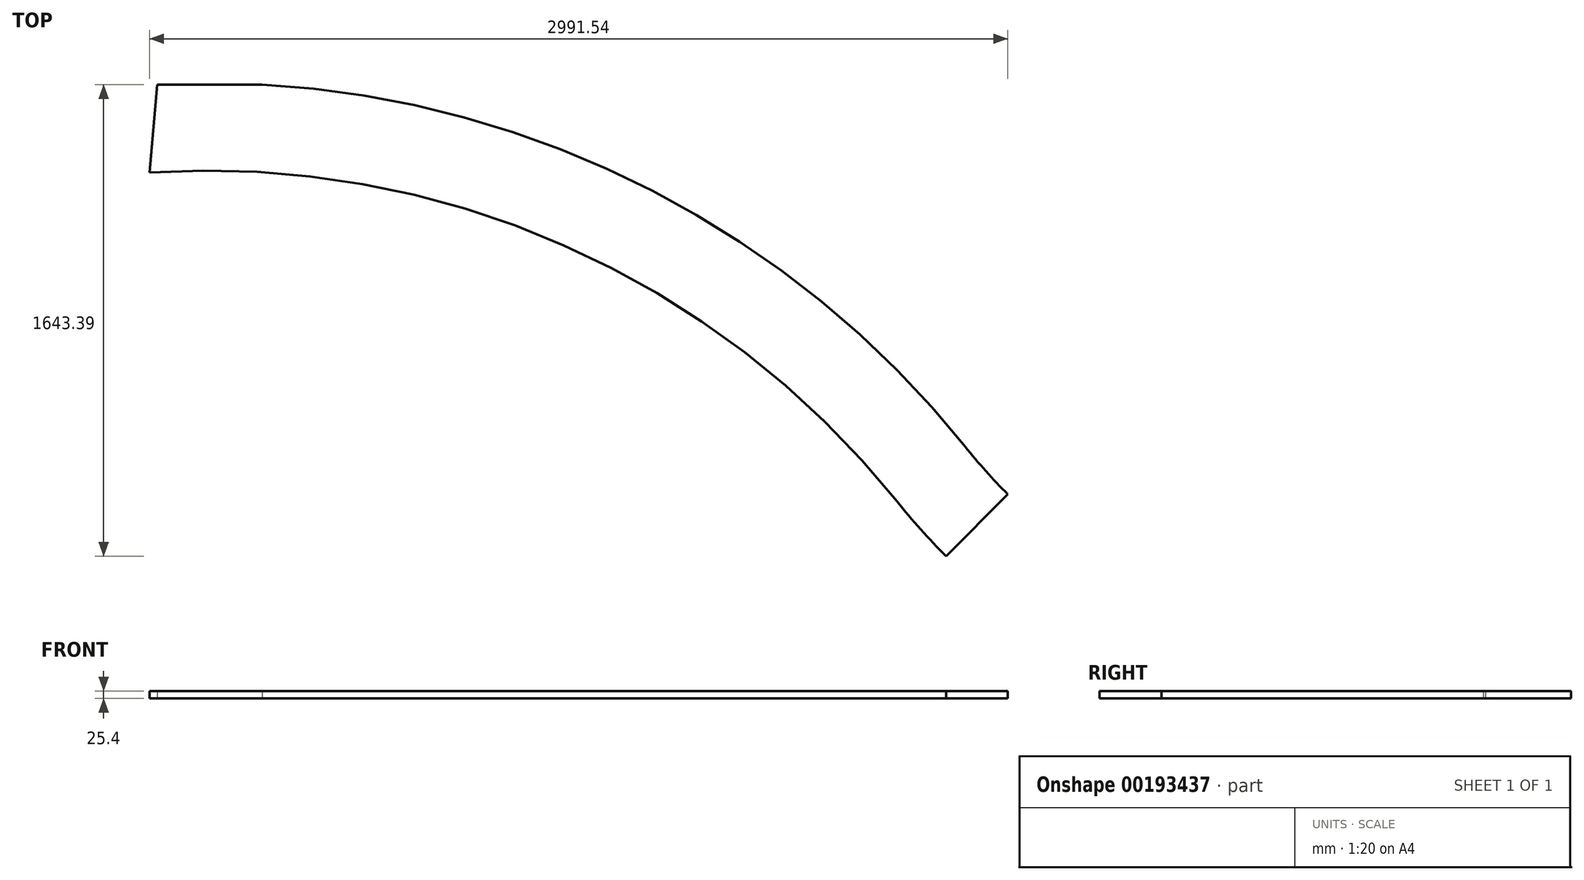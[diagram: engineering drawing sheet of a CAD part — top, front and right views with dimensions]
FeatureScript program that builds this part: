
annotation { "Feature Type Name" : "Feature", "Feature Type Description" : "" }
export const myFeature = defineFeature(function(context is Context, id is Id, definition is map)
    precondition{}
    {
        {
            var Q0;
            Q0=qCreatedBy(makeId("Top.planeOp"),FACE);
            var sketch = newSketch(context, id + "F0", { "sketchPlane" : qUnion([Q0])});
            skLineSegment(sketch, "E0", {"start": v(-2322.3, 99.74) * mm, "end": v(363.78, 99.74) * mm});
            skLineSegment(sketch, "E1", {"start": v(2078.28, -1614.76) * mm, "end": v(2078.28, -2224.36) * mm});
            skArc(sketch, "E2", {"start": v(2078.28, -1614.76) * mm, "mid": v(865.95, -1112.6) * mm, "end": v(363.78, 99.74) * mm});
            skArc(sketch, "E3.0", {"start": v(2078.28, -1919.56) * mm, "mid": v(1203.8, -1720.4) * mm, "end": v(501.84, -1162.16) * mm});
            skArc(sketch, "E4.0", {"start": v(2078.28, -2224.36) * mm, "mid": v(1071.81, -1995.13) * mm, "end": v(263.88, -1352.64) * mm});
            skLineSegment(sketch, "E5", {"start": v(-2322.3, 99.74) * mm, "end": v(-2341.12, -206.78) * mm});
            skPoint(sketch, "E6", {"position": v(-2322.3, 99.74) * mm});
            skArc(sketch, "E7", {"start": v(501.84, -1162.16) * mm, "mid": v(-757.31, -188.98) * mm, "end": v(-2322.3, 99.74) * mm});
            skArc(sketch, "E8.0", {"start": v(263.88, -1352.64) * mm, "mid": v(-898, -460.02) * mm, "end": v(-2341.12, -206.78) * mm});
            skPoint(sketch, "E9.orphan", {"position": v(-2399.79, -1162.16) * mm});
            skLineSegment(sketch, "E10", {"start": v(2078.28, 99.74) * mm, "end": v(0, -1978.55) * mm});
            skLineSegment(sketch, "E11", {"start": v(-2341.12, -206.78) * mm, "end": v(-2322.3, 99.74) * mm});
            skLineSegment(sketch, "E12", {"start": v(2078.28, -1614.76) * mm, "end": v(2052.9, -1614.09) * mm});
            skLineSegment(sketch, "E13.0", {"start": v(2052.88, -1614.09) * mm, "end": v(2052.88, -2223.26) * mm});
            skLineSegment(sketch, "E14", {"start": v(-2339.55, -181.22) * mm, "end": v(-2322.3, 99.74) * mm});
            skLineSegment(sketch, "E15", {"start": v(-2341.12, -206.78) * mm, "end": v(-2314.2, 100.17) * mm});
            skSolve(sketch);
        }
        {
            var Q0;
            {var subQ9=sQuery(id+"F0.wireOp",EDGE,"E8.0");Q0=makeQuery(id+"F0.imprint","IMPRINT",FACE,{"disambiguationData":[TD([[makeQuery(id+"F0.imprint","IMPRINT",EDGE,{"derivedFrom":subQ9}),-1.0]])]});}
            extrude(context, id + "F1", {"entities" : qUnion([Q0]), "depth" : 25.4 * mm});
        }
    });
